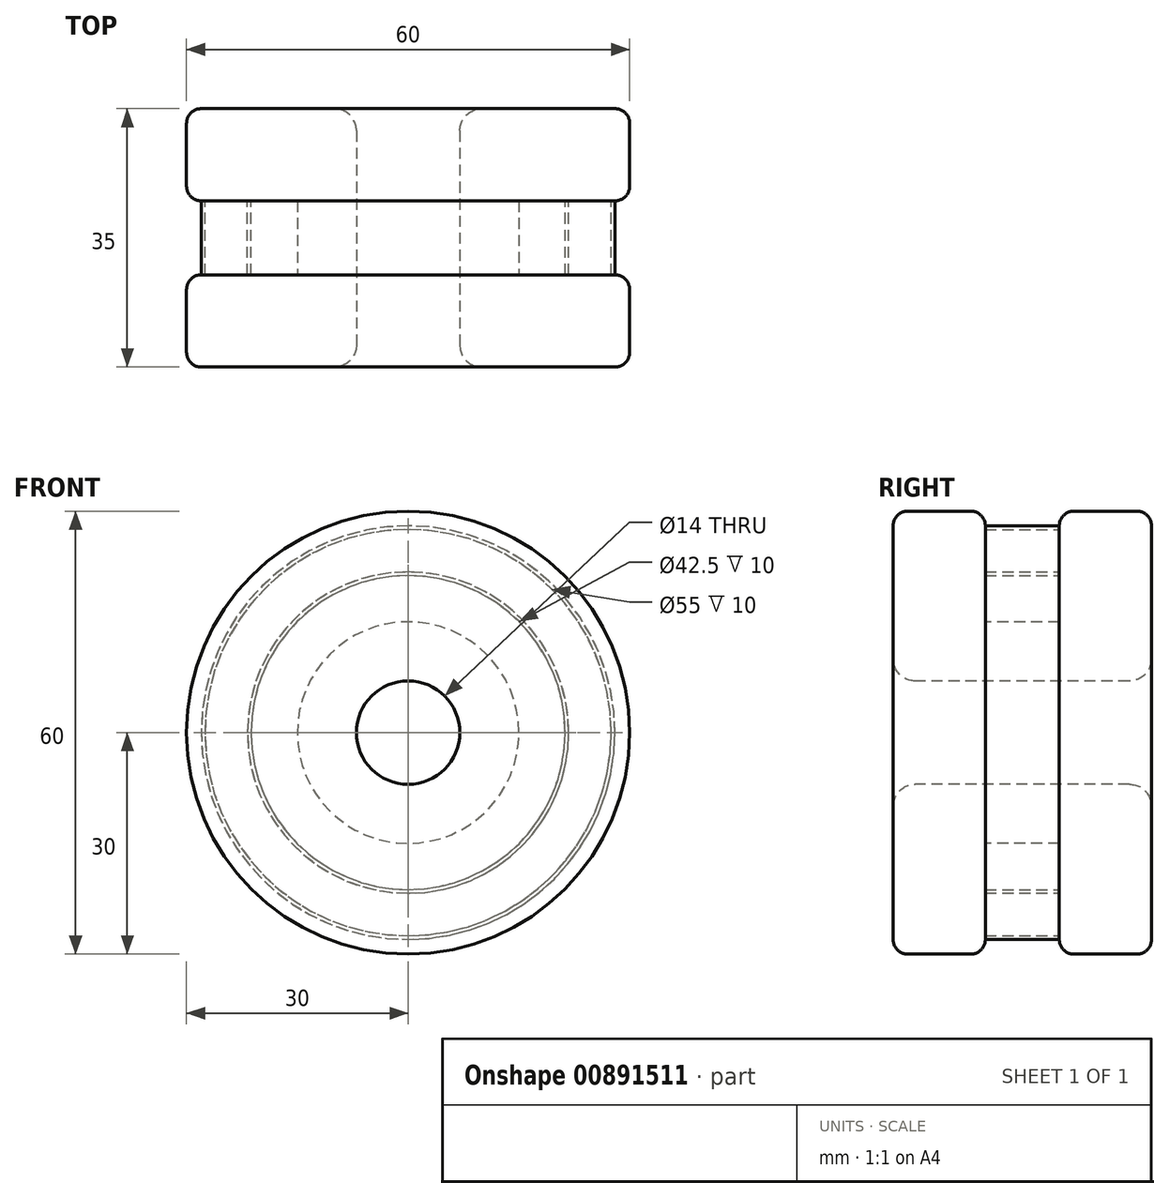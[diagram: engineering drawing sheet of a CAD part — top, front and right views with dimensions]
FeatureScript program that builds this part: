
annotation { "Feature Type Name" : "Feature", "Feature Type Description" : "" }
export const myFeature = defineFeature(function(context is Context, id is Id, definition is map)
    precondition{}
    {
        {
            var Q0;
            Q0=qCreatedBy(makeId("Top.planeOp"),FACE);
            var sketch = newSketch(context, id + "F0", { "sketchPlane" : qUnion([Q0])});
            skLineSegment(sketch, "E0", {"start": v(0, 0) * mm, "end": v(0, 35) * mm, "construction": true});
            skLineSegment(sketch, "E1", {"start": v(-7, 0) * mm, "end": v(-30, 0) * mm});
            skLineSegment(sketch, "E2", {"start": v(-30, 0) * mm, "end": v(-30, 12.5) * mm});
            skLineSegment(sketch, "E3", {"start": v(-30, 12.5) * mm, "end": v(-15, 12.5) * mm});
            skLineSegment(sketch, "E4", {"start": v(-15, 12.5) * mm, "end": v(-15, 22.5) * mm});
            skLineSegment(sketch, "E5", {"start": v(-15, 22.5) * mm, "end": v(-30, 22.5) * mm});
            skLineSegment(sketch, "E6", {"start": v(-30, 22.5) * mm, "end": v(-30, 35) * mm});
            skLineSegment(sketch, "E7", {"start": v(-30, 35) * mm, "end": v(-7, 35) * mm});
            skLineSegment(sketch, "E8", {"start": v(-7, 35) * mm, "end": v(-7, 0) * mm});
            skSolve(sketch);
        }
        {
            var Q0;
            Q0=makeQuery(id+"F0.imprint","IMPRINT",FACE,{"disambiguationData":[TD([[makeQuery(id+"F0.imprint","IMPRINT",EDGE,{"derivedFrom":sQuery(id+"F0.wireOp",EDGE,"E1")}),-1.0]])]});
            var Q1;
            Q1=sQuery(id+"F0.wireOp",EDGE,"E0");
            revolve(context, id + "F1", {"surfaceOperationType" : NewSurfaceOperationType.NEW, "entities" : qUnion([Q0]), "axis" : qUnion([Q1]), "revolveType" : RevolveType.FULL});
        }
        {
            var Q0;
            Q0=makeQuery(id+"F1.opRevolve","SWEPT_EDGE",EDGE,{"disambiguationData":[OSD([sQuery(id+"F0.wireOp",EDGE,"E5"),sQuery(id+"F0.wireOp",EDGE,"E6")])]});
            var Q1;
            Q1=makeQuery(id+"F1.opRevolve","SWEPT_EDGE",EDGE,{"disambiguationData":[OSD([sQuery(id+"F0.wireOp",EDGE,"E2"),sQuery(id+"F0.wireOp",EDGE,"E3")])]});
            var Q2;
            Q2=makeQuery(id+"F1.opRevolve","SWEPT_EDGE",EDGE,{"disambiguationData":[OSD([sQuery(id+"F0.wireOp",EDGE,"E6"),sQuery(id+"F0.wireOp",EDGE,"E7")])]});
            var Q3;
            Q3=makeQuery(id+"F1.opRevolve","SWEPT_EDGE",EDGE,{"disambiguationData":[OSD([sQuery(id+"F0.wireOp",EDGE,"E1"),sQuery(id+"F0.wireOp",EDGE,"E2")])]});
            fillet(context, id + "F2", {"entities" : qUnion([Q0, Q1, Q2, Q3]), "radius" : 2 * mm, "tangentPropagation" : true, "allowEdgeOverflow" : false});
        }
        {
            var Q0;
            Q0=makeQuery(id+"F1.opRevolve","SWEPT_EDGE",EDGE,{"disambiguationData":[OSD([sQuery(id+"F0.wireOp",EDGE,"E1"),sQuery(id+"F0.wireOp",EDGE,"E8")])]});
            var Q1;
            Q1=makeQuery(id+"F1.opRevolve","SWEPT_EDGE",EDGE,{"disambiguationData":[OSD([sQuery(id+"F0.wireOp",EDGE,"E7"),sQuery(id+"F0.wireOp",EDGE,"E8")])]});
            fillet(context, id + "F3", {"entities" : qUnion([Q0, Q1]), "radius" : 3 * mm, "tangentPropagation" : true, "allowEdgeOverflow" : false});
        }
        {
            var Q0;
            Q0=makeQuery(id+"F1.opRevolve","SWEPT_FACE",FACE,{"disambiguationData":[OSD([sQuery(id+"F0.wireOp",EDGE,"E5")])]});
            var sketch = newSketch(context, id + "F4", { "sketchPlane" : qUnion([Q0])});
            skCircle(sketch, "E9.0", {"center": v(0, 0) * mm, "radius": 28 * mm});
            skCircle(sketch, "E10.0", {"center": v(0, 0) * mm, "radius": 27.5 * mm});
            skCircle(sketch, "E11.0", {"center": v(0, 0) * mm, "radius": 15 * mm});
            skLineSegment(sketch, "E12", {"start": v(15, 0) * mm, "end": v(27.5, 0) * mm, "construction": true});
            skLineSegment(sketch, "E13", {"start": v(0, 0) * mm, "end": v(15, 0) * mm});
            skLineSegment(sketch, "E14", {"start": v(21.25, 0) * mm, "end": v(15, 0) * mm, "construction": true});
            skCircle(sketch, "E15", {"center": v(0, 0) * mm, "radius": 21.25 * mm});
            skCircle(sketch, "E16.0", {"center": v(0, 0) * mm, "radius": 21.75 * mm});
            skSolve(sketch);
        }
        {
            var Q0;
            Q0=makeQuery(id+"F4.imprint","IMPRINT",FACE,{"disambiguationData":[TD([[makeQuery(id+"F4.imprint","IMPRINT",EDGE,{"derivedFrom":sQuery(id+"F4.wireOp",EDGE,"E9.0")}),1.0]])]});
            var Q1;
            Q1=makeQuery(id+"F4.imprint","IMPRINT",FACE,{"disambiguationData":[TD([[makeQuery(id+"F4.imprint","IMPRINT",EDGE,{"derivedFrom":sQuery(id+"F4.wireOp",EDGE,"E15")}),-1.0]])]});
            var Q2;
            Q2=makeQuery(id+"F1.opRevolve","SWEPT_FACE",FACE,{"disambiguationData":[OSD([sQuery(id+"F0.wireOp",EDGE,"E3")])]});
            extrude(context, id + "F5", {"entities" : qUnion([Q0, Q1]), "operationType" : NewBodyOperationType.ADD, "endBound" : BoundingType.UP_TO_SURFACE, "depth" : 25 * mm, "endBoundEntityFace" : qUnion([Q2]), "offsetDistance" : 25 * mm});
        }
    });
